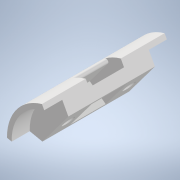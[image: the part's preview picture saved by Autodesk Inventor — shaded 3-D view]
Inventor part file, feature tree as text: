
AUTODESK INVENTOR PART (.ipt)
format: ipt  version: 2022 (Build 260153000, 153)  size: 195,584 bytes
history: native  units: mm
features: extrude x6, sketch x6, reference x6, other x5, projected_geometry x3, fillet x1
ambient origin geometry x8: Origin, YZ Plane, XZ Plane, XY Plane, X Axis, Y Axis, Z Axis, Center Point
bodies: Body1 (feature_tree)
feature tree (27):
  other  "Твердое тело1"
  extrude  "Выдавливание1"  Depth=0.2mm
  extrude  "Выдавливание2"  Depth=0.2mm
  extrude  "Выдавливание3"  Depth=34.0mm TaperAngle=0.0deg
  extrude  "Выдавливание4"  Depth=24.0mm TaperAngle=0.0deg
  fillet  "Сопряжение1"  Radius=2.5mm
  extrude  "Выдавливание5"  Depth=8.5mm
  extrude  "Выдавливание6"  Depth=4.95mm
  sketch  "Эскиз1"
  reference  "Ссылка1"
  reference  "Ссылка2"
  sketch  "Эскиз2"
  reference  "Ссылка3"
  reference  "Ссылка4"
  sketch  "Эскиз3"
  projected_geometry  "Спроецированная петля1"
  reference  "Ссылка5"
  sketch  "Эскиз4"
  projected_geometry  "Спроецированная петля2"
  sketch  "Эскиз5"
  reference  "Ссылка6"
  sketch  "Эскиз6"
  projected_geometry  "Спроецированная петля3"
  other  "<userpath>\Documents\Git\MZCAT_2024\MZCAT.iam"
  other  "MZCAT.iam"
  other  "base:1"
  other  "CAT_protector:1"
